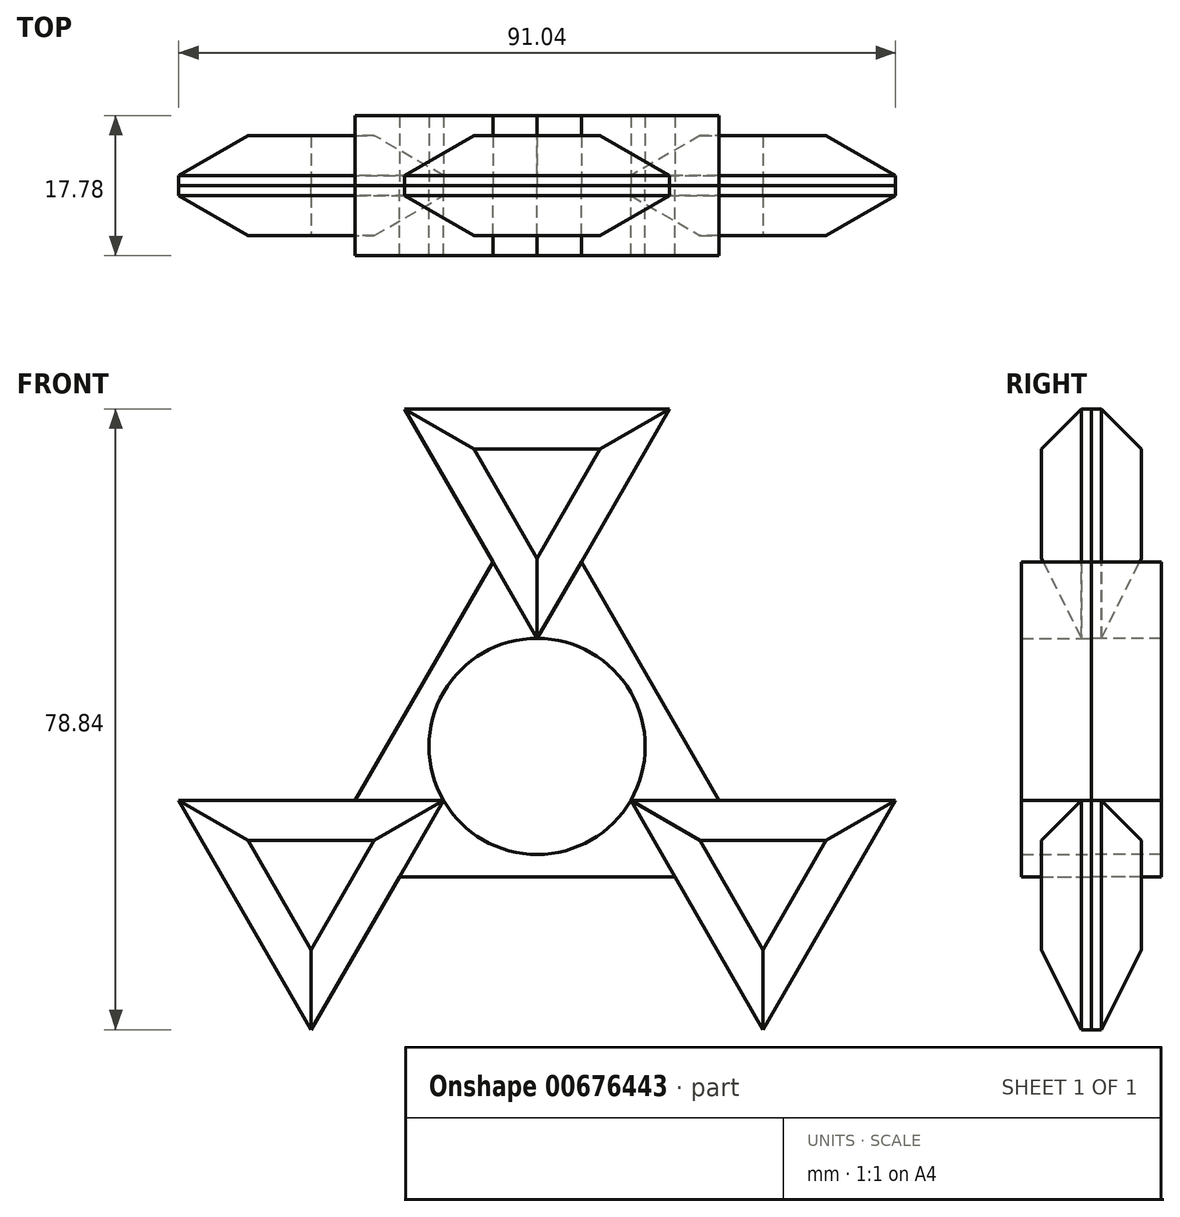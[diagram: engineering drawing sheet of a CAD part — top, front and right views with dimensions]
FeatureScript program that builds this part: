
annotation { "Feature Type Name" : "Feature", "Feature Type Description" : "" }
export const myFeature = defineFeature(function(context is Context, id is Id, definition is map)
    precondition{}
    {
        {
            var Q0;
            Q0=qCreatedBy(makeId("Front.planeOp"),FACE);
            var sketch = newSketch(context, id + "F0", { "sketchPlane" : qUnion([Q0])});
            skCircle(sketch, "E0.cCircle", {"center": v(0, 0) * mm, "radius": 33.14 * mm, "construction": true});
            skLineSegment(sketch, "E0.0", {"start": v(0, 33.14) * mm, "end": v(28.7, -16.57) * mm});
            skLineSegment(sketch, "E0.1", {"start": v(28.7, -16.57) * mm, "end": v(-28.7, -16.57) * mm});
            skLineSegment(sketch, "E0.2", {"start": v(-28.7, -16.57) * mm, "end": v(0, 33.14) * mm});
            skLineSegment(sketch, "E1", {"start": v(0, 0) * mm, "end": v(0, 33.14) * mm});
            skLineSegment(sketch, "E2", {"start": v(0, 0) * mm, "end": v(-28.7, -16.57) * mm});
            skLineSegment(sketch, "E3", {"start": v(0, 0) * mm, "end": v(28.7, -16.57) * mm});
            skCircle(sketch, "E4", {"center": v(0, 0) * mm, "radius": 13.73 * mm});
            skCircle(sketch, "E5.cCircle", {"center": v(28.7, -16.57) * mm, "radius": 19.41 * mm, "construction": true});
            skLineSegment(sketch, "E5.0", {"start": v(11.89, -6.86) * mm, "end": v(45.52, -6.86) * mm});
            skLineSegment(sketch, "E5.1", {"start": v(45.52, -6.86) * mm, "end": v(28.7, -35.99) * mm});
            skLineSegment(sketch, "E5.2", {"start": v(28.7, -35.99) * mm, "end": v(11.89, -6.86) * mm});
            skCircle(sketch, "E6.cCircle", {"center": v(0, 33.14) * mm, "radius": 19.41 * mm, "construction": true});
            skPoint(sketch, "E6.cCircle.perimeterSnap0", {"position": v(0, 16.57) * mm});
            skLineSegment(sketch, "E6.0", {"start": v(0, 13.73) * mm, "end": v(-16.81, 42.85) * mm});
            skPoint(sketch, "E6.0.startSnap0", {"position": v(0, 16.57) * mm});
            skLineSegment(sketch, "E6.1", {"start": v(-16.81, 42.85) * mm, "end": v(16.81, 42.85) * mm});
            skLineSegment(sketch, "E6.2", {"start": v(16.81, 42.85) * mm, "end": v(0, 13.73) * mm});
            skCircle(sketch, "E7.cCircle", {"center": v(-28.7, -16.57) * mm, "radius": 19.41 * mm, "construction": true});
            skLineSegment(sketch, "E7.0", {"start": v(-11.89, -6.86) * mm, "end": v(-28.7, -35.99) * mm});
            skLineSegment(sketch, "E7.1", {"start": v(-28.7, -35.99) * mm, "end": v(-45.52, -6.86) * mm});
            skLineSegment(sketch, "E7.2", {"start": v(-45.52, -6.86) * mm, "end": v(-11.89, -6.86) * mm});
            skSolve(sketch);
        }
        {
            var Q0;
            {var subQ0=sQuery(id+"F0.wireOp",EDGE,"E5.1");Q0=makeQuery(id+"F0.imprint","IMPRINT",FACE,{"disambiguationData":[TD([[makeQuery(id+"F0.imprint","IMPRINT",EDGE,{"derivedFrom":subQ0}),-1.0]])]});}
            var Q1;
            {var subQ1=sQuery(id+"F0.wireOp",EDGE,"E0.0");var subQ3=sQuery(id+"F0.wireOp",EDGE,"E5.0");var subQ4=makeQuery(id+"F0.imprint","INTERSECT",VERTEX,{"derivedFrom":[subQ1,subQ3]});Q1=makeQuery(id+"F0.imprint","IMPRINT",FACE,{"disambiguationData":[TD([[makeQuery(id+"F0.imprint","IMPRINT",EDGE,{"disambiguationData":[TD([[subQ4,-1.0]])],"derivedFrom":subQ1}),-1.0]])]});}
            var Q2;
            {var subQ1=sQuery(id+"F0.wireOp",EDGE,"E0.1");var subQ3=sQuery(id+"F0.wireOp",EDGE,"E5.2");var subQ4=makeQuery(id+"F0.imprint","INTERSECT",VERTEX,{"derivedFrom":[subQ1,subQ3]});Q2=makeQuery(id+"F0.imprint","IMPRINT",FACE,{"disambiguationData":[TD([[makeQuery(id+"F0.imprint","IMPRINT",EDGE,{"disambiguationData":[TD([[subQ4,1.0]])],"derivedFrom":subQ1}),-1.0]])]});}
            var Q3;
            {var subQ0=sQuery(id+"F0.wireOp",EDGE,"E7.1");Q3=makeQuery(id+"F0.imprint","IMPRINT",FACE,{"disambiguationData":[TD([[makeQuery(id+"F0.imprint","IMPRINT",EDGE,{"derivedFrom":subQ0}),-1.0]])]});}
            var Q4;
            {var subQ1=sQuery(id+"F0.wireOp",EDGE,"E0.2");var subQ3=sQuery(id+"F0.wireOp",EDGE,"E7.2");var subQ4=makeQuery(id+"F0.imprint","INTERSECT",VERTEX,{"derivedFrom":[subQ1,subQ3]});Q4=makeQuery(id+"F0.imprint","IMPRINT",FACE,{"disambiguationData":[TD([[makeQuery(id+"F0.imprint","IMPRINT",EDGE,{"disambiguationData":[TD([[subQ4,1.0]])],"derivedFrom":subQ1}),-1.0]])]});}
            var Q5;
            {var subQ1=sQuery(id+"F0.wireOp",EDGE,"E0.1");var subQ3=sQuery(id+"F0.wireOp",EDGE,"E7.0");var subQ4=makeQuery(id+"F0.imprint","INTERSECT",VERTEX,{"derivedFrom":[subQ1,subQ3]});Q5=makeQuery(id+"F0.imprint","IMPRINT",FACE,{"disambiguationData":[TD([[makeQuery(id+"F0.imprint","IMPRINT",EDGE,{"disambiguationData":[TD([[subQ4,-1.0]])],"derivedFrom":subQ1}),-1.0]])]});}
            var Q6;
            {var subQ1=sQuery(id+"F0.wireOp",EDGE,"E0.0");var subQ3=sQuery(id+"F0.wireOp",EDGE,"E6.2");var subQ4=makeQuery(id+"F0.imprint","INTERSECT",VERTEX,{"derivedFrom":[subQ1,subQ3]});Q6=makeQuery(id+"F0.imprint","IMPRINT",FACE,{"disambiguationData":[TD([[makeQuery(id+"F0.imprint","IMPRINT",EDGE,{"disambiguationData":[TD([[subQ4,1.0]])],"derivedFrom":subQ1}),-1.0]])]});}
            var Q7;
            {var subQ1=sQuery(id+"F0.wireOp",EDGE,"E0.2");var subQ3=sQuery(id+"F0.wireOp",EDGE,"E6.0");var subQ4=makeQuery(id+"F0.imprint","INTERSECT",VERTEX,{"derivedFrom":[subQ1,subQ3]});Q7=makeQuery(id+"F0.imprint","IMPRINT",FACE,{"disambiguationData":[TD([[makeQuery(id+"F0.imprint","IMPRINT",EDGE,{"disambiguationData":[TD([[subQ4,-1.0]])],"derivedFrom":subQ1}),-1.0]])]});}
            var Q8;
            {var subQ0=sQuery(id+"F0.wireOp",EDGE,"E6.1");Q8=makeQuery(id+"F0.imprint","IMPRINT",FACE,{"disambiguationData":[TD([[makeQuery(id+"F0.imprint","IMPRINT",EDGE,{"derivedFrom":subQ0}),-1.0]])]});}
            extrude(context, id + "F1", {"entities" : qUnion([Q0, Q1, Q2, Q3, Q4, Q5, Q6, Q7, Q8]), "depth" : 6.35 * mm, "offsetDistance" : 25.4 * mm});
        }
        {
            var Q0;
            {var subQ0=sQuery(id+"F0.wireOp",EDGE,"E6.2");var subQ1=sQuery(id+"F0.wireOp",EDGE,"E0.0");var subQ2=makeQuery(id+"F0.imprint","INTERSECT",VERTEX,{"derivedFrom":[subQ1,subQ0]});Q0=makeQuery(id+"F0.imprint","IMPRINT",FACE,{"disambiguationData":[TD([[makeQuery(id+"F0.imprint","IMPRINT",EDGE,{"disambiguationData":[TD([[subQ2,-1.0]])],"derivedFrom":subQ1}),-1.0]])]});}
            var Q1;
            {var subQ0=sQuery(id+"F0.wireOp",EDGE,"E5.2");var subQ1=sQuery(id+"F0.wireOp",EDGE,"E0.1");var subQ2=makeQuery(id+"F0.imprint","INTERSECT",VERTEX,{"derivedFrom":[subQ1,subQ0]});Q1=makeQuery(id+"F0.imprint","IMPRINT",FACE,{"disambiguationData":[TD([[makeQuery(id+"F0.imprint","IMPRINT",EDGE,{"disambiguationData":[TD([[subQ2,-1.0]])],"derivedFrom":subQ1}),-1.0]])]});}
            var Q2;
            {var subQ0=sQuery(id+"F0.wireOp",EDGE,"E7.2");var subQ1=sQuery(id+"F0.wireOp",EDGE,"E0.2");var subQ2=makeQuery(id+"F0.imprint","INTERSECT",VERTEX,{"derivedFrom":[subQ1,subQ0]});Q2=makeQuery(id+"F0.imprint","IMPRINT",FACE,{"disambiguationData":[TD([[makeQuery(id+"F0.imprint","IMPRINT",EDGE,{"disambiguationData":[TD([[subQ2,-1.0]])],"derivedFrom":subQ1}),-1.0]])]});}
            extrude(context, id + "F2", {"entities" : qUnion([Q0, Q1, Q2]), "depth" : 8.9 * mm, "offsetDistance" : 25.4 * mm});
        }
        {
            var Q0;
            Q0=makeQuery(id+"F1.opExtrude","CAP_EDGE",EDGE,{"disambiguationData":[OSD([sQuery(id+"F0.wireOp",EDGE,"E6.0")])],"isStart":false});
            var Q1;
            Q1=makeQuery(id+"F1.opExtrude","CAP_EDGE",EDGE,{"disambiguationData":[OSD([sQuery(id+"F0.wireOp",EDGE,"E6.2")])],"isStart":false});
            var Q2;
            Q2=makeQuery(id+"F1.opExtrude","CAP_EDGE",EDGE,{"disambiguationData":[OSD([sQuery(id+"F0.wireOp",EDGE,"E5.0")])],"isStart":false});
            var Q3;
            Q3=makeQuery(id+"F1.opExtrude","CAP_EDGE",EDGE,{"disambiguationData":[OSD([sQuery(id+"F0.wireOp",EDGE,"E5.2")])],"isStart":false});
            var Q4;
            Q4=makeQuery(id+"F1.opExtrude","CAP_EDGE",EDGE,{"disambiguationData":[OSD([sQuery(id+"F0.wireOp",EDGE,"E7.0")])],"isStart":false});
            var Q5;
            Q5=makeQuery(id+"F1.opExtrude","CAP_EDGE",EDGE,{"disambiguationData":[OSD([sQuery(id+"F0.wireOp",EDGE,"E7.2")])],"isStart":false});
            var Q6;
            Q6=makeQuery(id+"F1.opExtrude","CAP_EDGE",EDGE,{"disambiguationData":[OSD([sQuery(id+"F0.wireOp",EDGE,"E7.1")])],"isStart":false});
            var Q7;
            Q7=makeQuery(id+"F1.opExtrude","CAP_EDGE",EDGE,{"disambiguationData":[OSD([sQuery(id+"F0.wireOp",EDGE,"E6.1")])],"isStart":false});
            chamfer(context, id + "F3", {"entities" : qUnion([Q0, Q1, Q2, Q3, Q4, Q5, Q6, Q7]), "width" : 5.08 * mm, "tangentPropagation" : true});
        }
        {
            var Q0;
            Q0=makeQuery(id+"F1.opExtrude","CAP_EDGE",EDGE,{"disambiguationData":[OSD([sQuery(id+"F0.wireOp",EDGE,"E5.1")])],"isStart":false});
            chamfer(context, id + "F4", {"entities" : qUnion([Q0]), "width" : 5.08 * mm, "tangentPropagation" : true});
        }
        {
            var Q0;
            {var subQ0=sQuery(id+"F0.wireOp",EDGE,"E5.1");Q0=makeQuery(id+"F0.imprint","IMPRINT",FACE,{"disambiguationData":[TD([[makeQuery(id+"F0.imprint","IMPRINT",EDGE,{"derivedFrom":subQ0}),-1.0]])]});}
            var Q1;
            {var subQ1=sQuery(id+"F0.wireOp",EDGE,"E0.1");var subQ3=sQuery(id+"F0.wireOp",EDGE,"E5.2");var subQ4=makeQuery(id+"F0.imprint","INTERSECT",VERTEX,{"derivedFrom":[subQ1,subQ3]});Q1=makeQuery(id+"F0.imprint","IMPRINT",FACE,{"disambiguationData":[TD([[makeQuery(id+"F0.imprint","IMPRINT",EDGE,{"disambiguationData":[TD([[subQ4,1.0]])],"derivedFrom":subQ1}),-1.0]])]});}
            var Q2;
            {var subQ1=sQuery(id+"F0.wireOp",EDGE,"E0.0");var subQ3=sQuery(id+"F0.wireOp",EDGE,"E5.0");var subQ4=makeQuery(id+"F0.imprint","INTERSECT",VERTEX,{"derivedFrom":[subQ1,subQ3]});Q2=makeQuery(id+"F0.imprint","IMPRINT",FACE,{"disambiguationData":[TD([[makeQuery(id+"F0.imprint","IMPRINT",EDGE,{"disambiguationData":[TD([[subQ4,-1.0]])],"derivedFrom":subQ1}),-1.0]])]});}
            var Q3;
            {var subQ0=sQuery(id+"F0.wireOp",EDGE,"E7.1");Q3=makeQuery(id+"F0.imprint","IMPRINT",FACE,{"disambiguationData":[TD([[makeQuery(id+"F0.imprint","IMPRINT",EDGE,{"derivedFrom":subQ0}),-1.0]])]});}
            var Q4;
            {var subQ1=sQuery(id+"F0.wireOp",EDGE,"E0.1");var subQ3=sQuery(id+"F0.wireOp",EDGE,"E7.0");var subQ4=makeQuery(id+"F0.imprint","INTERSECT",VERTEX,{"derivedFrom":[subQ1,subQ3]});Q4=makeQuery(id+"F0.imprint","IMPRINT",FACE,{"disambiguationData":[TD([[makeQuery(id+"F0.imprint","IMPRINT",EDGE,{"disambiguationData":[TD([[subQ4,-1.0]])],"derivedFrom":subQ1}),-1.0]])]});}
            var Q5;
            {var subQ1=sQuery(id+"F0.wireOp",EDGE,"E0.2");var subQ3=sQuery(id+"F0.wireOp",EDGE,"E7.2");var subQ4=makeQuery(id+"F0.imprint","INTERSECT",VERTEX,{"derivedFrom":[subQ1,subQ3]});Q5=makeQuery(id+"F0.imprint","IMPRINT",FACE,{"disambiguationData":[TD([[makeQuery(id+"F0.imprint","IMPRINT",EDGE,{"disambiguationData":[TD([[subQ4,1.0]])],"derivedFrom":subQ1}),-1.0]])]});}
            var Q6;
            {var subQ0=sQuery(id+"F0.wireOp",EDGE,"E6.1");Q6=makeQuery(id+"F0.imprint","IMPRINT",FACE,{"disambiguationData":[TD([[makeQuery(id+"F0.imprint","IMPRINT",EDGE,{"derivedFrom":subQ0}),-1.0]])]});}
            var Q7;
            {var subQ1=sQuery(id+"F0.wireOp",EDGE,"E0.2");var subQ3=sQuery(id+"F0.wireOp",EDGE,"E6.0");var subQ4=makeQuery(id+"F0.imprint","INTERSECT",VERTEX,{"derivedFrom":[subQ1,subQ3]});Q7=makeQuery(id+"F0.imprint","IMPRINT",FACE,{"disambiguationData":[TD([[makeQuery(id+"F0.imprint","IMPRINT",EDGE,{"disambiguationData":[TD([[subQ4,-1.0]])],"derivedFrom":subQ1}),-1.0]])]});}
            var Q8;
            {var subQ1=sQuery(id+"F0.wireOp",EDGE,"E0.0");var subQ3=sQuery(id+"F0.wireOp",EDGE,"E6.2");var subQ4=makeQuery(id+"F0.imprint","INTERSECT",VERTEX,{"derivedFrom":[subQ1,subQ3]});Q8=makeQuery(id+"F0.imprint","IMPRINT",FACE,{"disambiguationData":[TD([[makeQuery(id+"F0.imprint","IMPRINT",EDGE,{"disambiguationData":[TD([[subQ4,1.0]])],"derivedFrom":subQ1}),-1.0]])]});}
            extrude(context, id + "F5", {"entities" : qUnion([Q0, Q1, Q2, Q3, Q4, Q5, Q6, Q7, Q8]), "depth" : -6.35 * mm, "offsetDistance" : 25.4 * mm});
        }
        {
            var Q0;
            Q0=makeQuery(id+"F5.opExtrude","CAP_EDGE",EDGE,{"disambiguationData":[OSD([sQuery(id+"F0.wireOp",EDGE,"E5.1")])],"isStart":false});
            var Q1;
            Q1=makeQuery(id+"F5.opExtrude","CAP_EDGE",EDGE,{"disambiguationData":[OSD([sQuery(id+"F0.wireOp",EDGE,"E5.0")])],"isStart":false});
            var Q2;
            Q2=makeQuery(id+"F5.opExtrude","CAP_EDGE",EDGE,{"disambiguationData":[OSD([sQuery(id+"F0.wireOp",EDGE,"E5.2")])],"isStart":false});
            var Q3;
            Q3=makeQuery(id+"F5.opExtrude","CAP_EDGE",EDGE,{"disambiguationData":[OSD([sQuery(id+"F0.wireOp",EDGE,"E7.0")])],"isStart":false});
            var Q4;
            Q4=makeQuery(id+"F5.opExtrude","CAP_EDGE",EDGE,{"disambiguationData":[OSD([sQuery(id+"F0.wireOp",EDGE,"E7.1")])],"isStart":false});
            var Q5;
            Q5=makeQuery(id+"F5.opExtrude","CAP_EDGE",EDGE,{"disambiguationData":[OSD([sQuery(id+"F0.wireOp",EDGE,"E7.2")])],"isStart":false});
            var Q6;
            Q6=makeQuery(id+"F5.opExtrude","CAP_EDGE",EDGE,{"disambiguationData":[OSD([sQuery(id+"F0.wireOp",EDGE,"E6.0")])],"isStart":false});
            var Q7;
            Q7=makeQuery(id+"F5.opExtrude","CAP_EDGE",EDGE,{"disambiguationData":[OSD([sQuery(id+"F0.wireOp",EDGE,"E6.1")])],"isStart":false});
            var Q8;
            Q8=makeQuery(id+"F5.opExtrude","CAP_EDGE",EDGE,{"disambiguationData":[OSD([sQuery(id+"F0.wireOp",EDGE,"E6.2")])],"isStart":false});
            chamfer(context, id + "F6", {"entities" : qUnion([Q0, Q1, Q2, Q3, Q4, Q5, Q6, Q7, Q8]), "width" : 5.08 * mm, "tangentPropagation" : true});
        }
        {
            var Q0;
            {var subQ0=sQuery(id+"F0.wireOp",EDGE,"E7.2");var subQ1=sQuery(id+"F0.wireOp",EDGE,"E0.2");var subQ2=makeQuery(id+"F0.imprint","INTERSECT",VERTEX,{"derivedFrom":[subQ1,subQ0]});Q0=makeQuery(id+"F0.imprint","IMPRINT",FACE,{"disambiguationData":[TD([[makeQuery(id+"F0.imprint","IMPRINT",EDGE,{"disambiguationData":[TD([[subQ2,-1.0]])],"derivedFrom":subQ1}),-1.0]])]});}
            var Q1;
            {var subQ0=sQuery(id+"F0.wireOp",EDGE,"E5.2");var subQ1=sQuery(id+"F0.wireOp",EDGE,"E0.1");var subQ2=makeQuery(id+"F0.imprint","INTERSECT",VERTEX,{"derivedFrom":[subQ1,subQ0]});Q1=makeQuery(id+"F0.imprint","IMPRINT",FACE,{"disambiguationData":[TD([[makeQuery(id+"F0.imprint","IMPRINT",EDGE,{"disambiguationData":[TD([[subQ2,-1.0]])],"derivedFrom":subQ1}),-1.0]])]});}
            var Q2;
            {var subQ0=sQuery(id+"F0.wireOp",EDGE,"E6.2");var subQ1=sQuery(id+"F0.wireOp",EDGE,"E0.0");var subQ2=makeQuery(id+"F0.imprint","INTERSECT",VERTEX,{"derivedFrom":[subQ1,subQ0]});Q2=makeQuery(id+"F0.imprint","IMPRINT",FACE,{"disambiguationData":[TD([[makeQuery(id+"F0.imprint","IMPRINT",EDGE,{"disambiguationData":[TD([[subQ2,-1.0]])],"derivedFrom":subQ1}),-1.0]])]});}
            extrude(context, id + "F7", {"entities" : qUnion([Q0, Q1, Q2]), "depth" : -8.9 * mm, "offsetDistance" : 25.4 * mm});
        }
    });
